# Revit family: 876-00-001-DN50-350
name_source: partatom
category: Pipe Accessories
units: mm (PartAtom-declared; Revit-internal decimal feet)

## family parameters
Always vertical = Yes
Cut with Voids When Loaded = No
Part Type = Valve - Breaks Into
Round Connector Dimension = Use Diameter
Shared = No
Work Plane-Based = No

## types (14) — shared parameters
876-0050-00-11102012 = DN50_PN16
876-0065-00-11102012 = DN65_PN16
876-0080-00-11102012 = DN80_PN16
876-0100-00-11102012 = DN100_PN16
876-0125-00-11102012 = DN125_PN16
876-0150-00-11102012 = DN150_PN16
876-0200-00-01102012 = DN200_PN10
876-0200-00-11102012 = DN200_PN16
876-0250-00-01102012 = DN250_PN10
876-0250-00-11102012 = DN250_PN16
876-0300-00-01102012 = DN300_PN10
876-0300-00-11102012 = DN300_PN16
876-0350-00-01102012 = DN350_PN10
876-0350-00-11102012 = DN350_PN16
Description_ = AVK NOZZLE CHECK VALVE, SINGLE STEM
Search_table = 876-00-001-DN50-350
URL product pages = https://www.avkvalves.com

## per-type parameters (varying)
| type | Bodywall_thickness | D | D1 | D2 | DN | Flange_thickness | Flange_thickness_2 | Flange_thickness_3 | ID | L | L1 |
| DN050_PN16 | 35 mm  [stored 0.114829 ft] | 83 mm | 125 mm  [stored 0.410105 ft] | 50 mm  [stored 0.164042 ft] | 50 mm  [stored 0.164042 ft] | 10 mm  [stored 0.0328084 ft] | 5 mm  [stored 0.0164042 ft] | 15 mm  [stored 0.0492126 ft] | 25 mm  [stored 0.082021 ft] | 150 mm  [stored 0.492126 ft] | 8 mm  [stored 0.0262467 ft] |
| DN065_PN16 | 43 mm | 93 mm | 145 mm  [stored 0.475722 ft] | 59 mm | 65 mm  [stored 0.213255 ft] | 10 mm  [stored 0.0328084 ft] | 5 mm  [stored 0.0164042 ft] | 15 mm  [stored 0.0492126 ft] | 33 mm | 170 mm  [stored 0.557743 ft] | 15 mm  [stored 0.0492126 ft] |
| DN080_PN16 | 50 mm  [stored 0.164042 ft] | 100 mm  [stored 0.328084 ft] | 160 mm  [stored 0.524934 ft] | 66 mm  [stored 0.216535 ft] | 80 mm  [stored 0.262467 ft] | 10 mm  [stored 0.0328084 ft] | 5 mm  [stored 0.0164042 ft] | 15 mm  [stored 0.0492126 ft] | 40 mm  [stored 0.131234 ft] | 180 mm | 18 mm  [stored 0.0590551 ft] |
| DN100_PN16 | 60 mm  [stored 0.19685 ft] | 110 mm  [stored 0.360892 ft] | 180 mm | 78 mm  [stored 0.255906 ft] | 100 mm  [stored 0.328084 ft] | 10 mm  [stored 0.0328084 ft] | 5 mm  [stored 0.0164042 ft] | 15 mm  [stored 0.0492126 ft] | 50 mm  [stored 0.164042 ft] | 190 mm | 20 mm  [stored 0.0656168 ft] |
| DN125_PN16 | 73 mm | 125 mm  [stored 0.410105 ft] | 210 mm | 92 mm  [stored 0.301837 ft] | 125 mm  [stored 0.410105 ft] | 10 mm  [stored 0.0328084 ft] | 5 mm  [stored 0.0164042 ft] | 15 mm  [stored 0.0492126 ft] | 63 mm | 200 mm | 21 mm  [stored 0.0688976 ft] |
| DN150_PN16 | 85 mm  [stored 0.278871 ft] | 143 mm | 240 mm | 106 mm | 150 mm  [stored 0.492126 ft] | 10 mm  [stored 0.0328084 ft] | 5 mm  [stored 0.0164042 ft] | 15 mm  [stored 0.0492126 ft] | 75 mm | 210 mm | 25 mm  [stored 0.082021 ft] |
| DN200_PN10 | 110 mm  [stored 0.360892 ft] | 170 mm  [stored 0.557743 ft] | 295 mm | 133 mm  [stored 0.436352 ft] | 200 mm | 15 mm  [stored 0.0492126 ft] | 8 mm  [stored 0.0262467 ft] | 23 mm | 100 mm  [stored 0.328084 ft] | 230 mm | 30 mm  [stored 0.0984252 ft] |
| DN200_PN16 | 110 mm  [stored 0.360892 ft] | 170 mm  [stored 0.557743 ft] | 295 mm | 133 mm  [stored 0.436352 ft] | 200 mm | 15 mm  [stored 0.0492126 ft] | 8 mm  [stored 0.0262467 ft] | 23 mm | 100 mm  [stored 0.328084 ft] | 230 mm | 30 mm  [stored 0.0984252 ft] |
| DN250_PN10 | 135 mm  [stored 0.442913 ft] | 198 mm | 350 mm | 160 mm  [stored 0.524934 ft] | 250 mm | 15 mm  [stored 0.0492126 ft] | 8 mm  [stored 0.0262467 ft] | 23 mm | 125 mm  [stored 0.410105 ft] | 250 mm | 40 mm  [stored 0.131234 ft] |
| DN250_PN16 | 135 mm  [stored 0.442913 ft] | 203 mm | 355 mm | 160 mm  [stored 0.524934 ft] | 250 mm | 15 mm  [stored 0.0492126 ft] | 8 mm  [stored 0.0262467 ft] | 23 mm | 125 mm  [stored 0.410105 ft] | 250 mm | 40 mm  [stored 0.131234 ft] |
| DN300_PN10 | 160 mm  [stored 0.524934 ft] | 223 mm | 400 mm | 185 mm | 300 mm | 20 mm  [stored 0.0656168 ft] | 10 mm  [stored 0.0328084 ft] | 30 mm  [stored 0.0984252 ft] | 150 mm  [stored 0.492126 ft] | 270 mm | 45 mm  [stored 0.147638 ft] |
| DN300_PN16 | 160 mm  [stored 0.524934 ft] | 230 mm | 410 mm | 185 mm | 300 mm | 20 mm  [stored 0.0656168 ft] | 10 mm  [stored 0.0328084 ft] | 30 mm  [stored 0.0984252 ft] | 150 mm  [stored 0.492126 ft] | 270 mm | 45 mm  [stored 0.147638 ft] |
| DN350_PN10 | 185 mm | 253 mm | 460 mm | 215 mm | 350 mm | 20 mm  [stored 0.0656168 ft] | 10 mm  [stored 0.0328084 ft] | 30 mm  [stored 0.0984252 ft] | 175 mm | 290 mm | 50 mm  [stored 0.164042 ft] |
| DN350_PN16 | 185 mm | 260 mm | 470 mm | 215 mm | 350 mm | 20 mm  [stored 0.0656168 ft] | 10 mm  [stored 0.0328084 ft] | 30 mm  [stored 0.0984252 ft] | 175 mm | 290 mm | 50 mm  [stored 0.164042 ft] |

note: [stored X ft] marks values corroborated as IEEE doubles in the binary element streams (Revit-internal decimal feet)

## geometry (parser evidence)
native form markers: Sweep x9
no freeform markers — native parametric forms only
